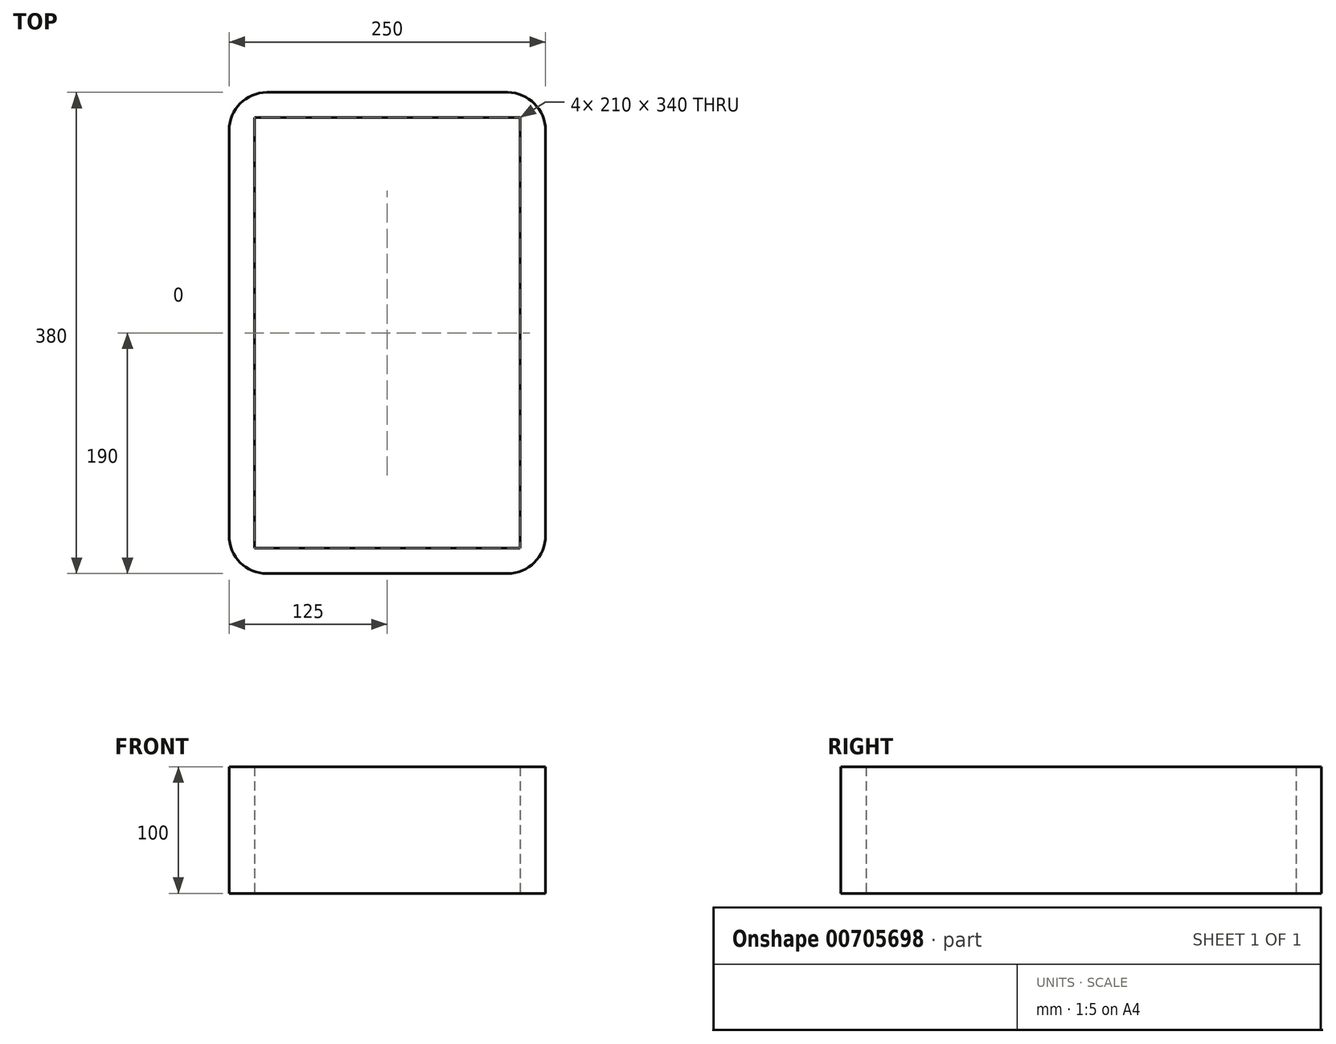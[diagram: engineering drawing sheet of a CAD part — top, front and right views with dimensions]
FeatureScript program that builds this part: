
annotation { "Feature Type Name" : "Feature", "Feature Type Description" : "" }
export const myFeature = defineFeature(function(context is Context, id is Id, definition is map)
    precondition{}
    {
        {
            var Q0;
            Q0=qCreatedBy(makeId("Top.planeOp"),FACE);
            var sketch = newSketch(context, id + "F0", { "sketchPlane" : qUnion([Q0])});
            skLineSegment(sketch, "E0.bottom", {"start": v(-30, 0) * mm, "end": v(-220, 0) * mm});
            skLineSegment(sketch, "E0.top", {"start": v(-30, 380) * mm, "end": v(-220, 380) * mm});
            skLineSegment(sketch, "E0.left", {"start": v(0, 30) * mm, "end": v(0, 350) * mm});
            skLineSegment(sketch, "E0.right", {"start": v(-250, 30) * mm, "end": v(-250, 350) * mm});
            skPoint(sketch, "E1.visualSharp", {"position": v(0, 380) * mm});
            skArc(sketch, "E1.filletArc", {"start": v(0, 350) * mm, "mid": v(-8.79, 371.21) * mm, "end": v(-30, 380) * mm});
            skPoint(sketch, "E2.visualSharp", {"position": v(-250, 380) * mm});
            skArc(sketch, "E2.filletArc", {"start": v(-220, 380) * mm, "mid": v(-241.21, 371.21) * mm, "end": v(-250, 350) * mm});
            skPoint(sketch, "E3.visualSharp", {"position": v(-250, 0) * mm});
            skArc(sketch, "E3.filletArc", {"start": v(-250, 30) * mm, "mid": v(-241.21, 8.79) * mm, "end": v(-220, 0) * mm});
            skPoint(sketch, "E4.visualSharp", {"position": v(0, 0) * mm});
            skArc(sketch, "E4.filletArc", {"start": v(-30, 0) * mm, "mid": v(-8.79, 8.79) * mm, "end": v(0, 30) * mm});
            skPoint(sketch, "E5", {"position": v(-20, 360) * mm});
            skPoint(sketch, "E6", {"position": v(-230, 360) * mm});
            skPoint(sketch, "E7", {"position": v(-20, 20) * mm});
            skPoint(sketch, "E8", {"position": v(-230, 20) * mm});
            skLineSegment(sketch, "E9", {"start": v(-20, 360) * mm, "end": v(-230, 360) * mm});
            skLineSegment(sketch, "E10", {"start": v(-230, 360) * mm, "end": v(-230, 20) * mm});
            skLineSegment(sketch, "E11", {"start": v(-20, 360) * mm, "end": v(-20, 20) * mm});
            skLineSegment(sketch, "E12", {"start": v(-20, 20) * mm, "end": v(-230, 20) * mm});
            skSolve(sketch);
        }
        {
            var Q0;
            Q0=makeQuery(id+"F0.imprint","IMPRINT",FACE,{"disambiguationData":[TD([[makeQuery(id+"F0.imprint","IMPRINT",EDGE,{"derivedFrom":sQuery(id+"F0.wireOp",EDGE,"E0.bottom")}),-1.0]])]});
            extrude(context, id + "F1", {"entities" : qUnion([Q0]), "depth" : 100 * mm, "offsetDistance" : 25.4 * mm});
        }
    });
